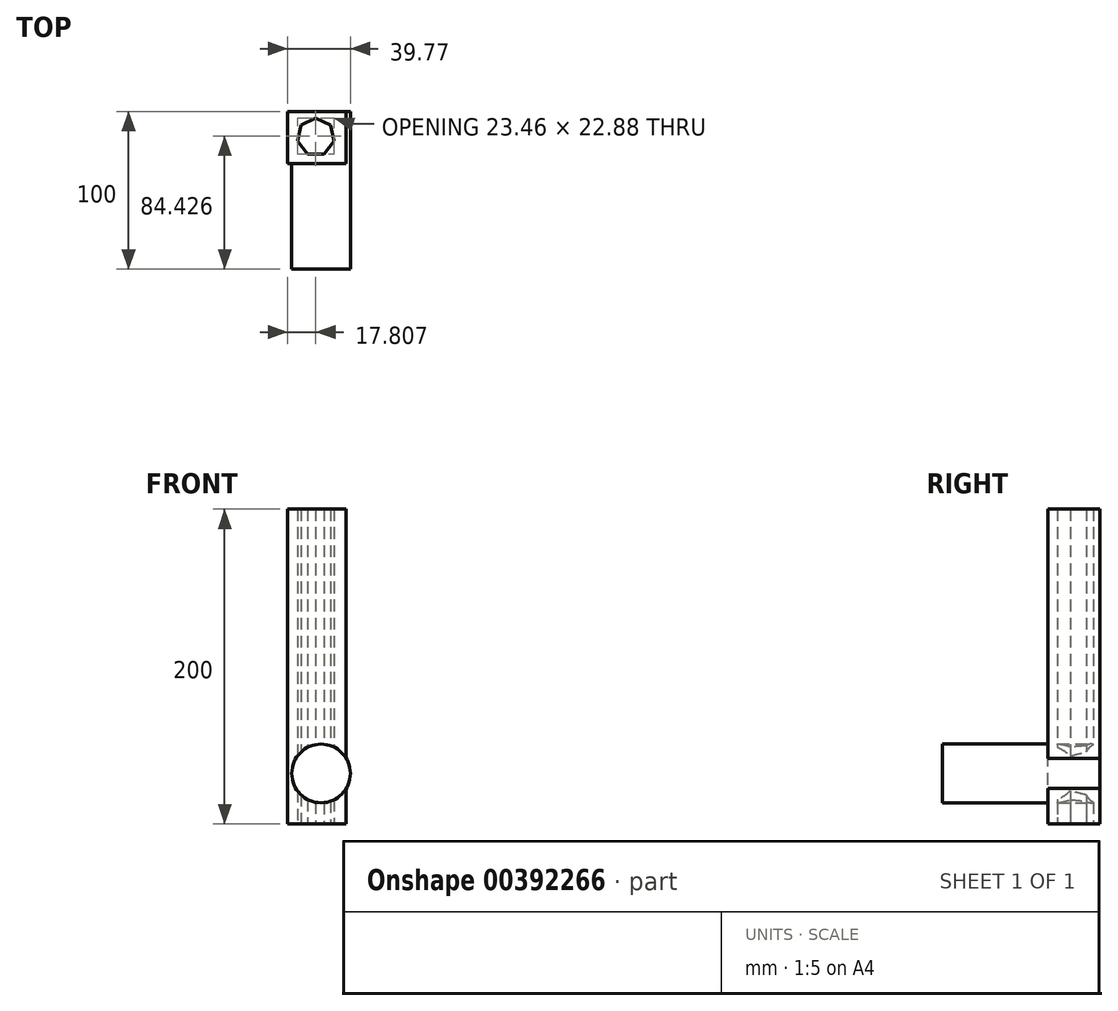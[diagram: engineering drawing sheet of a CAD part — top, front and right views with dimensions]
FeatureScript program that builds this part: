
annotation { "Feature Type Name" : "Feature", "Feature Type Description" : "" }
export const myFeature = defineFeature(function(context is Context, id is Id, definition is map)
    precondition{}
    {
        {
            var Q0;
            Q0=qCreatedBy(makeId("Top.planeOp"),FACE);
            var sketch = newSketch(context, id + "F0", { "sketchPlane" : qUnion([Q0])});
            skLineSegment(sketch, "E0.bottom", {"start": v(0, 33.02) * mm, "end": v(37.11, 33.02) * mm});
            skLineSegment(sketch, "E0.top", {"start": v(0, 0) * mm, "end": v(37.11, 0) * mm});
            skLineSegment(sketch, "E0.left", {"start": v(0, 33.02) * mm, "end": v(0, 0) * mm});
            skLineSegment(sketch, "E0.right", {"start": v(37.11, 33.02) * mm, "end": v(37.11, 0) * mm});
            skCircle(sketch, "E1.cCircle", {"center": v(17.8, 16.85) * mm, "radius": 10.84 * mm, "construction": true});
            skLineSegment(sketch, "E1.0", {"start": v(23.03, 6) * mm, "end": v(12.59, 6) * mm});
            skLineSegment(sketch, "E1.1", {"start": v(12.59, 6) * mm, "end": v(6.07, 14.17) * mm});
            skLineSegment(sketch, "E1.2", {"start": v(6.07, 14.17) * mm, "end": v(8.4, 24.35) * mm});
            skLineSegment(sketch, "E1.3", {"start": v(8.4, 24.35) * mm, "end": v(17.8, 28.88) * mm});
            skLineSegment(sketch, "E1.4", {"start": v(17.8, 28.88) * mm, "end": v(27.21, 24.35) * mm});
            skLineSegment(sketch, "E1.5", {"start": v(27.21, 24.35) * mm, "end": v(29.54, 14.17) * mm});
            skLineSegment(sketch, "E1.6", {"start": v(29.54, 14.17) * mm, "end": v(23.03, 6) * mm});
            skPoint(sketch, "E1.0.midPoint", {"position": v(17.8, 6) * mm});
            skSolve(sketch);
        }
        {
            var Q0;
            Q0 = qSketchRegion(id + "F0", true);
            extrude(context, id + "F1", {"entities" : qUnion([Q0]), "depth" : 200 * mm});
        }
        {
            var Q0;
            Q0=makeQuery(id+"F1.opExtrude","SWEPT_FACE",FACE,{"disambiguationData":[OSD([sQuery(id+"F0.wireOp",EDGE,"E0.bottom")])]});
            var sketch = newSketch(context, id + "F2", { "sketchPlane" : qUnion([Q0])});
            skCircle(sketch, "E2", {"center": v(-21.14, 32.11) * mm, "radius": 18.63 * mm});
            skSolve(sketch);
        }
        {
            var Q0;
            Q0 = qSketchRegion(id + "F2", true);
            extrude(context, id + "F3", {"entities" : qUnion([Q0]), "operationType" : NewBodyOperationType.ADD, "oppositeDirection" : true, "depth" : 100 * mm});
        }
    });
